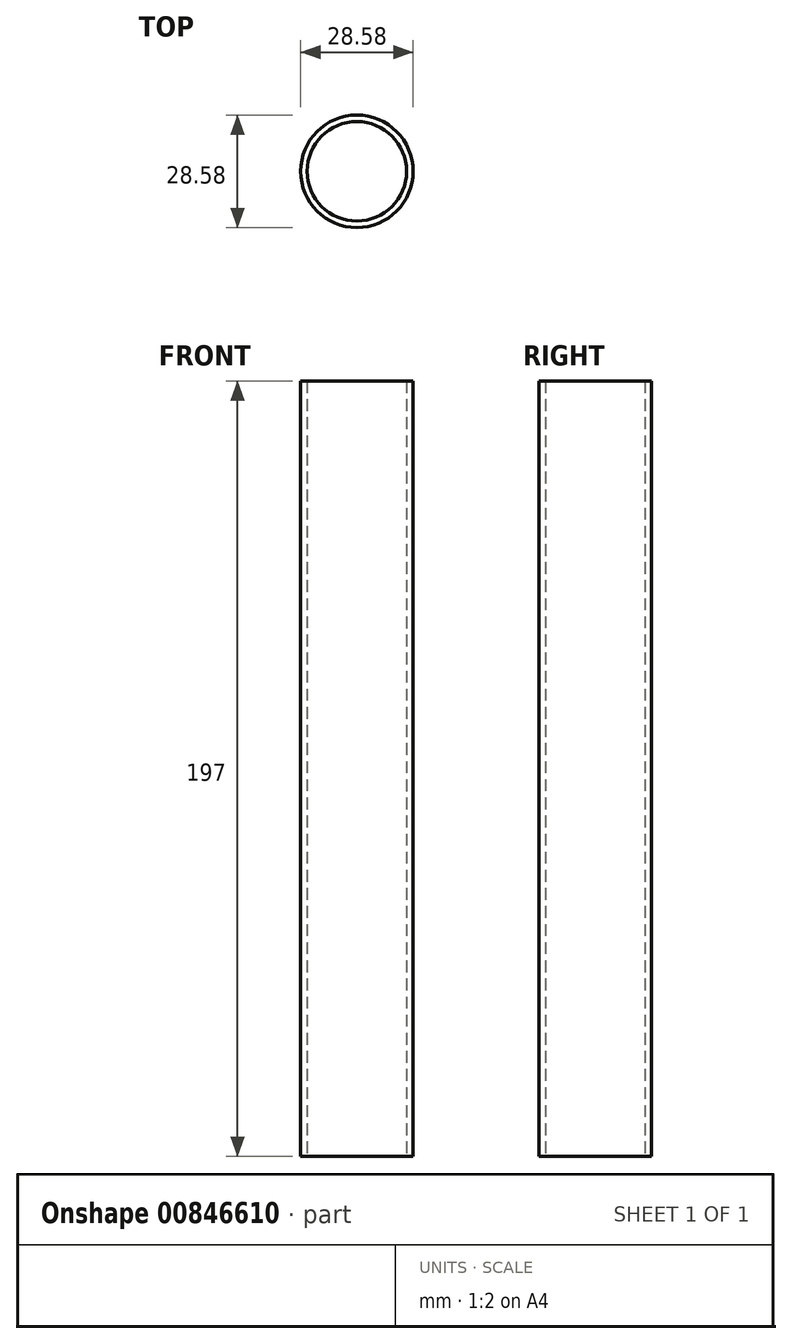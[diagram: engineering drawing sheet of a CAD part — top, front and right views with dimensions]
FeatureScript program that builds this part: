
annotation { "Feature Type Name" : "Feature", "Feature Type Description" : "" }
export const myFeature = defineFeature(function(context is Context, id is Id, definition is map)
    precondition{}
    {
        {
            var Q0;
            Q0=qCreatedBy(makeId("Top.planeOp"),FACE);
            var sketch = newSketch(context, id + "F0", { "sketchPlane" : qUnion([Q0])});
            skCircle(sketch, "E0", {"center": v(0, 0) * mm, "radius": 12.64 * mm});
            skCircle(sketch, "E1", {"center": v(0, 0) * mm, "radius": 14.29 * mm});
            skSolve(sketch);
        }
        {
            var Q0;
            Q0=makeQuery(id+"F0.imprint","IMPRINT",FACE,{"disambiguationData":[TD([[makeQuery(id+"F0.imprint","IMPRINT",EDGE,{"derivedFrom":sQuery(id+"F0.wireOp",EDGE,"E0")}),-1.0]])]});
            extrude(context, id + "F1", {"entities" : qUnion([Q0]), "depth" : 197 * mm, "offsetDistance" : 25.4 * mm});
        }
    });
